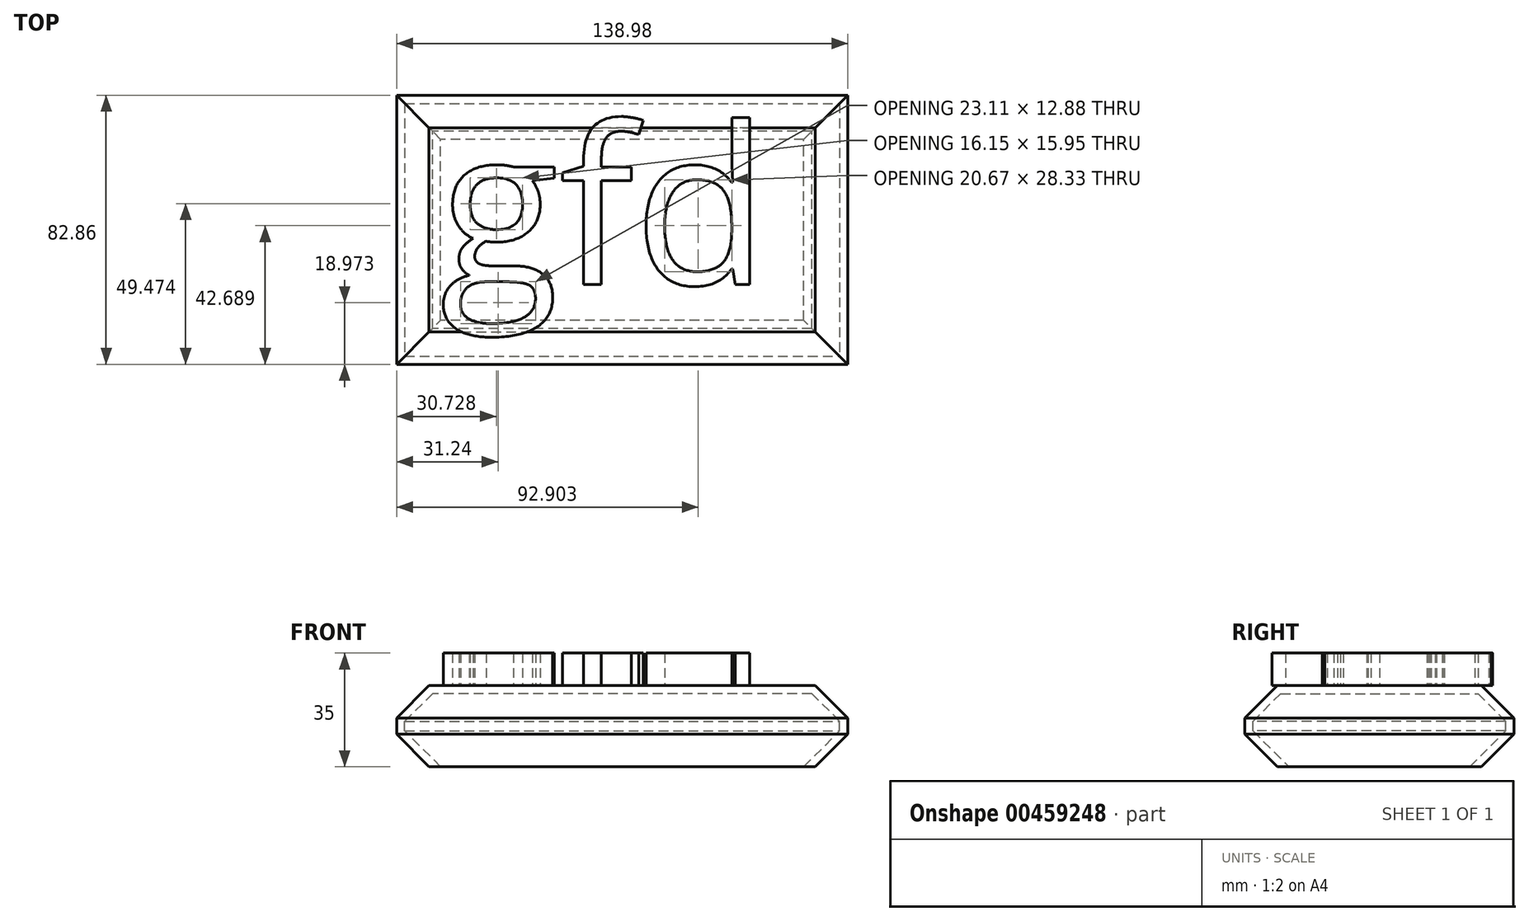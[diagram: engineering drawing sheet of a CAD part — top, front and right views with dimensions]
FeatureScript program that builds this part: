
annotation { "Feature Type Name" : "Feature", "Feature Type Description" : "" }
export const myFeature = defineFeature(function(context is Context, id is Id, definition is map)
    precondition{}
    {
        {
            var Q0;
            Q0=qCreatedBy(makeId("Top.planeOp"),FACE);
            var sketch = newSketch(context, id + "F0", { "sketchPlane" : qUnion([Q0])});
            skText(sketch, "E0", { "text": "gfd", "fontName": "OpenSans-Regular.ttf"});
            skLineSegment(sketch, "E1.bottom", {"start": v(-62.74, 31.37) * mm, "end": v(76.24, 31.37) * mm});
            skLineSegment(sketch, "E1.top", {"start": v(-62.74, -51.49) * mm, "end": v(76.24, -51.49) * mm});
            skLineSegment(sketch, "E1.left", {"start": v(-62.74, 31.37) * mm, "end": v(-62.74, -51.49) * mm});
            skLineSegment(sketch, "E1.right", {"start": v(76.24, 31.37) * mm, "end": v(76.24, -51.49) * mm});
            const initialGuessF0  = {"E0": [-0.04963, -0.0269, 1, 0, 0.0487]};
            skSetInitialGuess(sketch, initialGuessF0);
            skSolve(sketch);
        }
        {
            var Q0;
            Q0=makeQuery(id+"F0.imprint","IMPRINT",FACE,{"disambiguationData":[TD([[makeQuery(id+"F0.imprint","IMPRINT",EDGE,{"derivedFrom":sQuery(id+"F0.wireOp",EDGE,"E0.sketch_text.stroke-44")}),-1.0]])]});
            var Q1;
            Q1=makeQuery(id+"F0.imprint","IMPRINT",FACE,{"disambiguationData":[TD([[makeQuery(id+"F0.imprint","IMPRINT",EDGE,{"derivedFrom":sQuery(id+"F0.wireOp",EDGE,"E0.sketch_text.stroke-0")}),-1.0]])]});
            var Q2;
            Q2=makeQuery(id+"F0.imprint","IMPRINT",FACE,{"disambiguationData":[TD([[makeQuery(id+"F0.imprint","IMPRINT",EDGE,{"derivedFrom":sQuery(id+"F0.wireOp",EDGE,"E0.sketch_text.stroke-61")}),-1.0]])]});
            extrude(context, id + "F1", {"entities" : qUnion([Q0, Q1, Q2]), "depth" : 10 * mm});
        }
        {
            var Q0;
            Q0=makeQuery(id+"F0.imprint","IMPRINT",FACE,{"disambiguationData":[TD([[makeQuery(id+"F0.imprint","IMPRINT",EDGE,{"derivedFrom":sQuery(id+"F0.wireOp",EDGE,"E0.sketch_text.stroke-0")}),-1.0]])]});
            var Q1;
            Q1=makeQuery(id+"F0.imprint","IMPRINT",FACE,{"disambiguationData":[TD([[makeQuery(id+"F0.imprint","IMPRINT",EDGE,{"derivedFrom":sQuery(id+"F0.wireOp",EDGE,"E0.sketch_text.stroke-44")}),-1.0]])]});
            var Q2;
            Q2=makeQuery(id+"F0.imprint","IMPRINT",FACE,{"disambiguationData":[TD([[makeQuery(id+"F0.imprint","IMPRINT",EDGE,{"derivedFrom":sQuery(id+"F0.wireOp",EDGE,"E0.sketch_text.stroke-61")}),-1.0]])]});
            var Q3;
            Q3=makeQuery(id+"F0.imprint","IMPRINT",FACE,{"disambiguationData":[TD([[makeQuery(id+"F0.imprint","IMPRINT",EDGE,{"derivedFrom":sQuery(id+"F0.wireOp",EDGE,"E0.sketch_text.stroke-0")}),1.0]])]});
            var Q4;
            Q4=makeQuery(id+"F0.imprint","IMPRINT",FACE,{"disambiguationData":[TD([[makeQuery(id+"F0.imprint","IMPRINT",EDGE,{"derivedFrom":sQuery(id+"F0.wireOp",EDGE,"E0.sketch_text.stroke-76")}),1.0]])]});
            var Q5;
            Q5=makeQuery(id+"F0.imprint","IMPRINT",FACE,{"disambiguationData":[TD([[makeQuery(id+"F0.imprint","IMPRINT",EDGE,{"derivedFrom":sQuery(id+"F0.wireOp",EDGE,"E0.sketch_text.stroke-29")}),1.0]])]});
            var Q6;
            Q6=makeQuery(id+"F0.imprint","IMPRINT",FACE,{"disambiguationData":[TD([[makeQuery(id+"F0.imprint","IMPRINT",EDGE,{"derivedFrom":sQuery(id+"F0.wireOp",EDGE,"E0.sketch_text.stroke-38")}),1.0]])]});
            extrude(context, id + "F2", {"entities" : qUnion([Q0, Q1, Q2, Q3, Q4, Q5, Q6]), "oppositeDirection" : true, "depth" : 25 * mm});
        }
        {
            var Q0;
            Q0=makeQuery(id+"F2.opExtrude","CAP_EDGE",EDGE,{"disambiguationData":[OSD([sQuery(id+"F0.wireOp",EDGE,"E1.top")])],"isStart":true});
            var Q1;
            Q1=makeQuery(id+"F2.opExtrude","CAP_EDGE",EDGE,{"disambiguationData":[OSD([sQuery(id+"F0.wireOp",EDGE,"E1.top")])],"isStart":false});
            var Q2;
            Q2=makeQuery(id+"F2.opExtrude","CAP_EDGE",EDGE,{"disambiguationData":[OSD([sQuery(id+"F0.wireOp",EDGE,"E1.right")])],"isStart":false});
            var Q3;
            Q3=makeQuery(id+"F2.opExtrude","CAP_EDGE",EDGE,{"disambiguationData":[OSD([sQuery(id+"F0.wireOp",EDGE,"E1.right")])],"isStart":true});
            var Q4;
            Q4=makeQuery(id+"F2.opExtrude","CAP_EDGE",EDGE,{"disambiguationData":[OSD([sQuery(id+"F0.wireOp",EDGE,"E1.bottom")])],"isStart":true});
            var Q5;
            Q5=makeQuery(id+"F2.opExtrude","CAP_EDGE",EDGE,{"disambiguationData":[OSD([sQuery(id+"F0.wireOp",EDGE,"E1.bottom")])],"isStart":false});
            var Q6;
            Q6=makeQuery(id+"F2.opExtrude","CAP_EDGE",EDGE,{"disambiguationData":[OSD([sQuery(id+"F0.wireOp",EDGE,"E1.left")])],"isStart":false});
            var Q7;
            Q7=makeQuery(id+"F2.opExtrude","CAP_EDGE",EDGE,{"disambiguationData":[OSD([sQuery(id+"F0.wireOp",EDGE,"E1.left")])],"isStart":true});
            chamfer(context, id + "F3", {"entities" : qUnion([Q0, Q1, Q2, Q3, Q4, Q5, Q6, Q7]), "width" : 10 * mm, "tangentPropagation" : true});
        }
        {
            var Q0;
            Q0=makeQuery(id+"F2.opExtrude","CAP_FACE",FACE,{"disambiguationData":[OSD([sQuery(id+"F0.wireOp",EDGE,"E1.bottom"),sQuery(id+"F0.wireOp",EDGE,"E1.top"),sQuery(id+"F0.wireOp",EDGE,"E1.left"),sQuery(id+"F0.wireOp",EDGE,"E1.right")])],"isStart":false});
            shell(context, id + "F4", {"entities" : qUnion([Q0]), "thickness" : 2.5 * mm});
        }
    });
